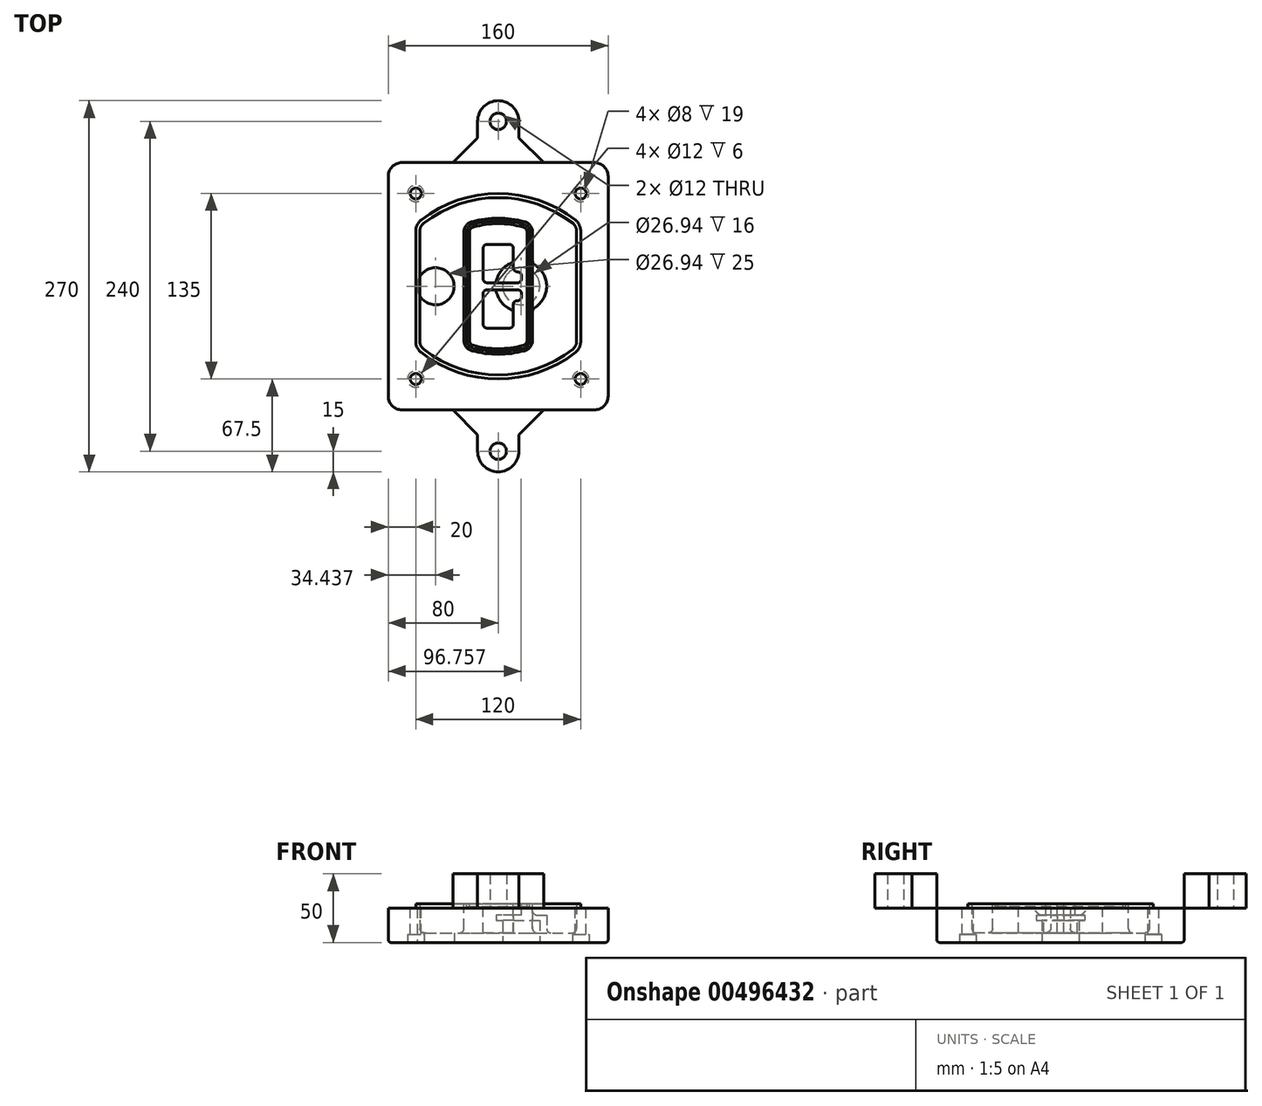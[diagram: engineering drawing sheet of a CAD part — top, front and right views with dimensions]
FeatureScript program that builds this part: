
annotation { "Feature Type Name" : "Feature", "Feature Type Description" : "" }
export const myFeature = defineFeature(function(context is Context, id is Id, definition is map)
    precondition{}
    {
        {
            var Q0;
            Q0=qCreatedBy(makeId("Top.planeOp"),FACE);
            var sketch = newSketch(context, id + "F0", { "sketchPlane" : qUnion([Q0])});
            skPoint(sketch, "E0.rect.middle", {"position": v(0, 0) * mm});
            skLineSegment(sketch, "E1.bottom", {"start": v(-70, -90) * mm, "end": v(70, -90) * mm});
            skLineSegment(sketch, "E1.top", {"start": v(-70, 90) * mm, "end": v(70, 90) * mm});
            skLineSegment(sketch, "E1.left", {"start": v(-80, -80) * mm, "end": v(-80, 80) * mm});
            skLineSegment(sketch, "E1.right", {"start": v(80, -80) * mm, "end": v(80, 80) * mm});
            skLineSegment(sketch, "E2", {"start": v(-80, 90) * mm, "end": v(80, -90) * mm, "construction": true});
            skLineSegment(sketch, "E3", {"start": v(80, 90) * mm, "end": v(-80, -90) * mm, "construction": true});
            skCircle(sketch, "E4", {"center": v(-60, 67.5) * mm, "radius": 4 * mm});
            skCircle(sketch, "E5", {"center": v(60, 67.5) * mm, "radius": 4 * mm});
            skCircle(sketch, "E6", {"center": v(60, -67.5) * mm, "radius": 4 * mm});
            skCircle(sketch, "E7", {"center": v(-60, -67.5) * mm, "radius": 4 * mm});
            skLineSegment(sketch, "E8", {"start": v(-60, 67.5) * mm, "end": v(60, 67.5) * mm, "construction": true});
            skLineSegment(sketch, "E9", {"start": v(60, 67.5) * mm, "end": v(60, -67.5) * mm, "construction": true});
            skLineSegment(sketch, "E10", {"start": v(60, -67.5) * mm, "end": v(-60, -67.5) * mm, "construction": true});
            skLineSegment(sketch, "E11", {"start": v(-60, -67.5) * mm, "end": v(-60, 67.5) * mm, "construction": true});
            skLineSegment(sketch, "E12", {"start": v(-60, 40.3) * mm, "end": v(-60, -40.3) * mm});
            skLineSegment(sketch, "E13", {"start": v(60, 40.3) * mm, "end": v(60, -40.3) * mm});
            skArc(sketch, "E14", {"start": v(56.15, 48.18) * mm, "mid": v(0, 67.5) * mm, "end": v(-56.15, 48.18) * mm});
            skArc(sketch, "E15", {"start": v(-56.15, -48.18) * mm, "mid": v(0, -67.5) * mm, "end": v(56.15, -48.18) * mm});
            skLineSegment(sketch, "E16", {"start": v(-60, 0) * mm, "end": v(60, 0) * mm, "construction": true});
            skPoint(sketch, "E17.visualSharp", {"position": v(-60, -45) * mm});
            skArc(sketch, "E17.filletArc", {"start": v(-60, -40.3) * mm, "mid": v(-58.99, -44.68) * mm, "end": v(-56.15, -48.18) * mm});
            skPoint(sketch, "E18.visualSharp", {"position": v(-60, 45) * mm});
            skArc(sketch, "E18.filletArc", {"start": v(-56.15, 48.18) * mm, "mid": v(-58.99, 44.68) * mm, "end": v(-60, 40.3) * mm});
            skPoint(sketch, "E19.visualSharp", {"position": v(60, 45) * mm});
            skArc(sketch, "E19.filletArc", {"start": v(60, 40.3) * mm, "mid": v(58.99, 44.68) * mm, "end": v(56.15, 48.18) * mm});
            skPoint(sketch, "E20.visualSharp", {"position": v(60, -45) * mm});
            skArc(sketch, "E20.filletArc", {"start": v(56.15, -48.18) * mm, "mid": v(58.99, -44.68) * mm, "end": v(60, -40.3) * mm});
            skPoint(sketch, "E21.visualSharp", {"position": v(-80, 90) * mm});
            skArc(sketch, "E21.filletArc", {"start": v(-70, 90) * mm, "mid": v(-77.07, 87.07) * mm, "end": v(-80, 80) * mm});
            skPoint(sketch, "E22.visualSharp", {"position": v(80, 90) * mm});
            skArc(sketch, "E22.filletArc", {"start": v(80, 80) * mm, "mid": v(77.07, 87.07) * mm, "end": v(70, 90) * mm});
            skPoint(sketch, "E23.visualSharp", {"position": v(80, -90) * mm});
            skArc(sketch, "E23.filletArc", {"start": v(70, -90) * mm, "mid": v(77.07, -87.07) * mm, "end": v(80, -80) * mm});
            skPoint(sketch, "E24.visualSharp", {"position": v(-80, -90) * mm});
            skArc(sketch, "E24.filletArc", {"start": v(-80, -80) * mm, "mid": v(-77.07, -87.07) * mm, "end": v(-70, -90) * mm});
            skArc(sketch, "E25.0", {"start": v(57, 40.3) * mm, "mid": v(56.3, 43.36) * mm, "end": v(54.3, 45.81) * mm});
            skLineSegment(sketch, "E25.1", {"start": v(57, 40.3) * mm, "end": v(57, -40.3) * mm});
            skArc(sketch, "E25.2", {"start": v(54.3, -45.81) * mm, "mid": v(56.3, -43.36) * mm, "end": v(57, -40.3) * mm});
            skArc(sketch, "E25.3", {"start": v(-54.3, -45.81) * mm, "mid": v(0, -64.5) * mm, "end": v(54.3, -45.81) * mm});
            skArc(sketch, "E25.4", {"start": v(-57, -40.3) * mm, "mid": v(-56.3, -43.36) * mm, "end": v(-54.3, -45.81) * mm});
            skArc(sketch, "E25.5", {"start": v(54.3, 45.81) * mm, "mid": v(0, 64.5) * mm, "end": v(-54.3, 45.81) * mm});
            skLineSegment(sketch, "E25.6", {"start": v(-57, 40.3) * mm, "end": v(-57, -40.3) * mm});
            skArc(sketch, "E25.7", {"start": v(-54.3, 45.81) * mm, "mid": v(-56.3, 43.36) * mm, "end": v(-57, 40.3) * mm});
            skArc(sketch, "E26.0", {"start": v(-58.62, 51.33) * mm, "mid": v(-62.58, 46.43) * mm, "end": v(-64, 40.3) * mm});
            skArc(sketch, "E26.1", {"start": v(58.62, 51.33) * mm, "mid": v(0, 71.5) * mm, "end": v(-58.62, 51.33) * mm});
            skArc(sketch, "E26.2", {"start": v(64, 40.3) * mm, "mid": v(62.58, 46.43) * mm, "end": v(58.62, 51.33) * mm});
            skLineSegment(sketch, "E26.3", {"start": v(64, 40.3) * mm, "end": v(64, -40.3) * mm});
            skArc(sketch, "E26.4", {"start": v(58.62, -51.33) * mm, "mid": v(62.58, -46.43) * mm, "end": v(64, -40.3) * mm});
            skLineSegment(sketch, "E26.5", {"start": v(-64, 40.3) * mm, "end": v(-64, -40.3) * mm});
            skArc(sketch, "E26.6", {"start": v(-58.62, -51.33) * mm, "mid": v(0, -71.5) * mm, "end": v(58.62, -51.33) * mm});
            skArc(sketch, "E26.7", {"start": v(-64, -40.3) * mm, "mid": v(-62.58, -46.43) * mm, "end": v(-58.62, -51.33) * mm});
            skSolve(sketch);
        }
        {
            var Q0;
            Q0=makeQuery(id+"F0.imprint","IMPRINT",FACE,{"disambiguationData":[TD([[makeQuery(id+"F0.imprint","IMPRINT",EDGE,{"derivedFrom":sQuery(id+"F0.wireOp",EDGE,"E1.bottom")}),1.0]])]});
            var Q1;
            Q1=makeQuery(id+"F0.imprint","IMPRINT",FACE,{"disambiguationData":[TD([[makeQuery(id+"F0.imprint","IMPRINT",EDGE,{"derivedFrom":sQuery(id+"F0.wireOp",EDGE,"E12")}),1.0]])]});
            var Q2;
            Q2=makeQuery(id+"F0.imprint","IMPRINT",FACE,{"disambiguationData":[TD([[makeQuery(id+"F0.imprint","IMPRINT",EDGE,{"derivedFrom":sQuery(id+"F0.wireOp",EDGE,"E25.0")}),1.0]])]});
            var Q3;
            Q3=makeQuery(id+"F0.imprint","IMPRINT",FACE,{"disambiguationData":[TD([[makeQuery(id+"F0.imprint","IMPRINT",EDGE,{"derivedFrom":sQuery(id+"F0.wireOp",EDGE,"E12")}),-1.0]])]});
            extrude(context, id + "F1", {"entities" : qUnion([Q0, Q1, Q2, Q3]), "oppositeDirection" : true, "depth" : 25 * mm});
        }
        {
            var Q0;
            Q0=makeQuery(id+"F0.imprint","IMPRINT",FACE,{"disambiguationData":[TD([[makeQuery(id+"F0.imprint","IMPRINT",EDGE,{"derivedFrom":sQuery(id+"F0.wireOp",EDGE,"E12")}),1.0]])]});
            extrude(context, id + "F2", {"entities" : qUnion([Q0]), "operationType" : NewBodyOperationType.ADD, "depth" : 3 * mm});
        }
        {
            var Q0;
            Q0=makeQuery(id+"F0.imprint","IMPRINT",FACE,{"disambiguationData":[TD([[makeQuery(id+"F0.imprint","IMPRINT",EDGE,{"derivedFrom":sQuery(id+"F0.wireOp",EDGE,"E25.0")}),1.0]])]});
            extrude(context, id + "F3", {"entities" : qUnion([Q0]), "operationType" : NewBodyOperationType.REMOVE, "oppositeDirection" : true, "depth" : 18 * mm});
        }
        {
            var Q0;
            Q0=makeQuery(id+"F2.opExtrude","CAP_FACE",FACE,{"disambiguationData":[OSD([sQuery(id+"F0.wireOp",EDGE,"E12"),sQuery(id+"F0.wireOp",EDGE,"E13"),sQuery(id+"F0.wireOp",EDGE,"E14"),sQuery(id+"F0.wireOp",EDGE,"E15"),sQuery(id+"F0.wireOp",EDGE,"E17.filletArc"),sQuery(id+"F0.wireOp",EDGE,"E18.filletArc"),sQuery(id+"F0.wireOp",EDGE,"E19.filletArc"),sQuery(id+"F0.wireOp",EDGE,"E20.filletArc"),sQuery(id+"F0.wireOp",EDGE,"E25.0"),sQuery(id+"F0.wireOp",EDGE,"E25.1"),sQuery(id+"F0.wireOp",EDGE,"E25.2"),sQuery(id+"F0.wireOp",EDGE,"E25.3"),sQuery(id+"F0.wireOp",EDGE,"E25.4"),sQuery(id+"F0.wireOp",EDGE,"E25.5"),sQuery(id+"F0.wireOp",EDGE,"E25.6"),sQuery(id+"F0.wireOp",EDGE,"E25.7")])],"isStart":false});
            var sketch = newSketch(context, id + "F4", { "sketchPlane" : qUnion([Q0])});
            skArc(sketch, "E27.0", {"start": v(-19.08, -46.97) * mm, "mid": v(0, -49.5) * mm, "end": v(19.08, -46.97) * mm});
            skArc(sketch, "E28.0", {"start": v(19.08, 46.97) * mm, "mid": v(0, 49.5) * mm, "end": v(-19.08, 46.97) * mm});
            skLineSegment(sketch, "E29", {"start": v(-25, 39.25) * mm, "end": v(-25, -39.25) * mm});
            skLineSegment(sketch, "E30", {"start": v(25, 39.25) * mm, "end": v(25, -39.25) * mm});
            skLineSegment(sketch, "E31", {"start": v(-25, 45.1) * mm, "end": v(25, 45.1) * mm, "construction": true});
            skLineSegment(sketch, "E32", {"start": v(-25, -45.1) * mm, "end": v(25, -45.1) * mm, "construction": true});
            skPoint(sketch, "E33.visualSharp", {"position": v(-25, 45.1) * mm});
            skArc(sketch, "E33.filletArc", {"start": v(-19.08, 46.97) * mm, "mid": v(-23.35, 44.11) * mm, "end": v(-25, 39.25) * mm});
            skPoint(sketch, "E34.visualSharp", {"position": v(25, 45.1) * mm});
            skArc(sketch, "E34.filletArc", {"start": v(25, 39.25) * mm, "mid": v(23.35, 44.11) * mm, "end": v(19.08, 46.97) * mm});
            skPoint(sketch, "E35.visualSharp", {"position": v(25, -45.1) * mm});
            skArc(sketch, "E35.filletArc", {"start": v(19.08, -46.97) * mm, "mid": v(23.35, -44.11) * mm, "end": v(25, -39.25) * mm});
            skPoint(sketch, "E36.visualSharp", {"position": v(-25, -45.1) * mm});
            skArc(sketch, "E36.filletArc", {"start": v(-25, -39.25) * mm, "mid": v(-23.35, -44.11) * mm, "end": v(-19.08, -46.97) * mm});
            skArc(sketch, "E37.0", {"start": v(54.3, 45.81) * mm, "mid": v(0, 64.5) * mm, "end": v(-54.3, 45.81) * mm});
            skArc(sketch, "E37.1", {"start": v(-54.3, 45.81) * mm, "mid": v(-56.3, 43.36) * mm, "end": v(-57, 40.3) * mm});
            skLineSegment(sketch, "E37.2", {"start": v(-57, 40.3) * mm, "end": v(-57, -40.3) * mm});
            skArc(sketch, "E37.3", {"start": v(-57, -40.3) * mm, "mid": v(-56.3, -43.36) * mm, "end": v(-54.3, -45.81) * mm});
            skArc(sketch, "E37.4", {"start": v(-54.3, -45.81) * mm, "mid": v(0, -64.5) * mm, "end": v(54.3, -45.81) * mm});
            skArc(sketch, "E37.5", {"start": v(54.3, -45.81) * mm, "mid": v(56.3, -43.36) * mm, "end": v(57, -40.3) * mm});
            skLineSegment(sketch, "E37.6", {"start": v(57, 40.3) * mm, "end": v(57, -40.3) * mm});
            skArc(sketch, "E37.7", {"start": v(57, 40.3) * mm, "mid": v(56.3, 43.36) * mm, "end": v(54.3, 45.81) * mm});
            skLineSegment(sketch, "E38.0", {"start": v(23, 39.25) * mm, "end": v(23, -39.25) * mm});
            skArc(sketch, "E38.1", {"start": v(18.56, -45.04) * mm, "mid": v(21.76, -42.9) * mm, "end": v(23, -39.25) * mm});
            skArc(sketch, "E38.2", {"start": v(-18.56, -45.04) * mm, "mid": v(0, -47.5) * mm, "end": v(18.56, -45.04) * mm});
            skArc(sketch, "E38.3", {"start": v(-23, -39.25) * mm, "mid": v(-21.76, -42.9) * mm, "end": v(-18.56, -45.04) * mm});
            skLineSegment(sketch, "E38.4", {"start": v(-23, 39.25) * mm, "end": v(-23, -39.25) * mm});
            skArc(sketch, "E38.5", {"start": v(23, 39.25) * mm, "mid": v(21.76, 42.9) * mm, "end": v(18.56, 45.04) * mm});
            skArc(sketch, "E38.6", {"start": v(-18.56, 45.04) * mm, "mid": v(-21.76, 42.9) * mm, "end": v(-23, 39.25) * mm});
            skArc(sketch, "E38.7", {"start": v(18.56, 45.04) * mm, "mid": v(0, 47.5) * mm, "end": v(-18.56, 45.04) * mm});
            skArc(sketch, "E39.0", {"start": v(21, 39.25) * mm, "mid": v(20.18, 41.68) * mm, "end": v(18.04, 43.1) * mm});
            skLineSegment(sketch, "E39.1", {"start": v(21, 39.25) * mm, "end": v(21, -39.25) * mm});
            skArc(sketch, "E39.2", {"start": v(18.04, -43.1) * mm, "mid": v(20.18, -41.68) * mm, "end": v(21, -39.25) * mm});
            skArc(sketch, "E39.3", {"start": v(-18.04, -43.1) * mm, "mid": v(0, -45.5) * mm, "end": v(18.04, -43.1) * mm});
            skArc(sketch, "E39.4", {"start": v(-21, -39.25) * mm, "mid": v(-20.18, -41.68) * mm, "end": v(-18.04, -43.1) * mm});
            skArc(sketch, "E39.5", {"start": v(18.04, 43.1) * mm, "mid": v(0, 45.5) * mm, "end": v(-18.04, 43.1) * mm});
            skLineSegment(sketch, "E39.6", {"start": v(-21, 39.25) * mm, "end": v(-21, -39.25) * mm});
            skArc(sketch, "E39.7", {"start": v(-18.04, 43.1) * mm, "mid": v(-20.18, 41.68) * mm, "end": v(-21, 39.25) * mm});
            skLineSegment(sketch, "E40", {"start": v(-25, 0) * mm, "end": v(25, 0) * mm, "construction": true});
            skLineSegment(sketch, "E41", {"start": v(-11, 5.5) * mm, "end": v(-11, 27.5) * mm});
            skLineSegment(sketch, "E42", {"start": v(-8, 30.5) * mm, "end": v(8, 30.5) * mm});
            skLineSegment(sketch, "E43", {"start": v(11, 27.5) * mm, "end": v(11, 13.5) * mm});
            skLineSegment(sketch, "E44", {"start": v(14, 10.5) * mm, "end": v(14, 10.5) * mm});
            skLineSegment(sketch, "E45", {"start": v(17, 7.5) * mm, "end": v(17, 5.5) * mm});
            skLineSegment(sketch, "E46", {"start": v(14, 2.5) * mm, "end": v(-8, 2.5) * mm});
            skPoint(sketch, "E47.visualSharp", {"position": v(-11, 30.5) * mm});
            skArc(sketch, "E47.filletArc", {"start": v(-8, 30.5) * mm, "mid": v(-10.12, 29.62) * mm, "end": v(-11, 27.5) * mm});
            skPoint(sketch, "E48.visualSharp", {"position": v(11, 30.5) * mm});
            skArc(sketch, "E48.filletArc", {"start": v(11, 27.5) * mm, "mid": v(10.12, 29.62) * mm, "end": v(8, 30.5) * mm});
            skPoint(sketch, "E49.visualSharp", {"position": v(11, 10.5) * mm});
            skArc(sketch, "E49.filletArc", {"start": v(11, 13.5) * mm, "mid": v(11.88, 11.38) * mm, "end": v(14, 10.5) * mm});
            skPoint(sketch, "E50.visualSharp", {"position": v(17, 10.5) * mm});
            skArc(sketch, "E50.filletArc", {"start": v(17, 7.5) * mm, "mid": v(16.12, 9.62) * mm, "end": v(14, 10.5) * mm});
            skPoint(sketch, "E51.visualSharp", {"position": v(17, 2.5) * mm});
            skArc(sketch, "E51.filletArc", {"start": v(14, 2.5) * mm, "mid": v(16.12, 3.38) * mm, "end": v(17, 5.5) * mm});
            skPoint(sketch, "E52.visualSharp", {"position": v(-11, 2.5) * mm});
            skArc(sketch, "E52.filletArc", {"start": v(-11, 5.5) * mm, "mid": v(-10.12, 3.38) * mm, "end": v(-8, 2.5) * mm});
            skLineSegment(sketch, "E53.0.MirrorCS", {"start": v(14, -2.5) * mm, "end": v(-8, -2.5) * mm});
            skArc(sketch, "E54.0.MirrorCS", {"start": v(-11, -5.5) * mm, "mid": v(-10.12, -3.38) * mm, "end": v(-8, -2.5) * mm});
            skLineSegment(sketch, "E55.0.MirrorCS", {"start": v(-11, -5.5) * mm, "end": v(-11, -27.5) * mm});
            skArc(sketch, "E56.0.MirrorCS", {"start": v(-8, -30.5) * mm, "mid": v(-10.12, -29.62) * mm, "end": v(-11, -27.5) * mm});
            skLineSegment(sketch, "E57.0.MirrorCS", {"start": v(-8, -30.5) * mm, "end": v(8, -30.5) * mm});
            skArc(sketch, "E58.0.MirrorCS", {"start": v(11, -27.5) * mm, "mid": v(10.12, -29.62) * mm, "end": v(8, -30.5) * mm});
            skLineSegment(sketch, "E59.0.MirrorCS", {"start": v(11, -27.5) * mm, "end": v(11, -13.5) * mm});
            skArc(sketch, "E60.0.MirrorCS", {"start": v(11, -13.5) * mm, "mid": v(11.88, -11.38) * mm, "end": v(14, -10.5) * mm});
            skArc(sketch, "E61.0.MirrorCS", {"start": v(17, -7.5) * mm, "mid": v(16.12, -9.62) * mm, "end": v(14, -10.5) * mm});
            skLineSegment(sketch, "E62.0.MirrorCS", {"start": v(17, -7.5) * mm, "end": v(17, -5.5) * mm});
            skArc(sketch, "E63.0.MirrorCS", {"start": v(14, -2.5) * mm, "mid": v(16.12, -3.38) * mm, "end": v(17, -5.5) * mm});
            skSolve(sketch);
        }
        {
            var Q0;
            Q0=makeQuery(id+"F4.imprint","IMPRINT",FACE,{"disambiguationData":[TD([[makeQuery(id+"F4.imprint","IMPRINT",EDGE,{"derivedFrom":sQuery(id+"F4.wireOp",EDGE,"E27.0")}),1.0]])]});
            var Q1;
            Q1=makeQuery(id+"F4.imprint","IMPRINT",FACE,{"disambiguationData":[TD([[makeQuery(id+"F4.imprint","IMPRINT",EDGE,{"derivedFrom":sQuery(id+"F4.wireOp",EDGE,"E38.0")}),-1.0]])]});
            var Q2;
            Q2=makeQuery(id+"F4.imprint","IMPRINT",FACE,{"disambiguationData":[TD([[makeQuery(id+"F4.imprint","IMPRINT",EDGE,{"derivedFrom":sQuery(id+"F4.wireOp",EDGE,"E39.0")}),1.0]])]});
            extrude(context, id + "F5", {"entities" : qUnion([Q0, Q1, Q2]), "operationType" : NewBodyOperationType.ADD, "endBound" : BoundingType.UP_TO_NEXT, "oppositeDirection" : true, "depth" : 25 * mm});
        }
        {
            var Q0;
            Q0=makeQuery(id+"F4.imprint","IMPRINT",FACE,{"disambiguationData":[TD([[makeQuery(id+"F4.imprint","IMPRINT",EDGE,{"derivedFrom":sQuery(id+"F4.wireOp",EDGE,"E38.0")}),-1.0]])]});
            extrude(context, id + "F6", {"entities" : qUnion([Q0]), "operationType" : NewBodyOperationType.REMOVE, "oppositeDirection" : true, "depth" : 2 * mm});
        }
        {
            var Q0;
            Q0=makeQuery(id+"F1.opExtrude","CAP_FACE",FACE,{"disambiguationData":[OSD([sQuery(id+"F0.wireOp",EDGE,"E1.bottom"),sQuery(id+"F0.wireOp",EDGE,"E1.top"),sQuery(id+"F0.wireOp",EDGE,"E1.left"),sQuery(id+"F0.wireOp",EDGE,"E1.right"),sQuery(id+"F0.wireOp",EDGE,"E4"),sQuery(id+"F0.wireOp",EDGE,"E5"),sQuery(id+"F0.wireOp",EDGE,"E6"),sQuery(id+"F0.wireOp",EDGE,"E7"),sQuery(id+"F0.wireOp",EDGE,"E21.filletArc"),sQuery(id+"F0.wireOp",EDGE,"E22.filletArc"),sQuery(id+"F0.wireOp",EDGE,"E23.filletArc"),sQuery(id+"F0.wireOp",EDGE,"E24.filletArc")])],"isStart":false});
            var sketch = newSketch(context, id + "F7", { "sketchPlane" : qUnion([Q0])});
            skCircle(sketch, "E64", {"center": v(16.76, 0) * mm, "radius": 13.47 * mm});
            skCircle(sketch, "E65", {"center": v(-45.56, 0) * mm, "radius": 13.47 * mm});
            skLineSegment(sketch, "E66", {"start": v(80, 0) * mm, "end": v(-80, 0) * mm});
            skCircle(sketch, "E67", {"center": v(16.76, 0) * mm, "radius": 18.47 * mm});
            skCircle(sketch, "E68", {"center": v(60, -67.5) * mm, "radius": 6 * mm});
            skCircle(sketch, "E69", {"center": v(-60, -67.5) * mm, "radius": 6 * mm});
            skCircle(sketch, "E70", {"center": v(-60, 67.5) * mm, "radius": 6 * mm});
            skCircle(sketch, "E71", {"center": v(60, 67.5) * mm, "radius": 6 * mm});
            skSolve(sketch);
        }
        {
            var Q0;
            {var subQ1=sQuery(id+"F7.wireOp",EDGE,"E66");var subQ4=sQuery(id+"F7.wireOp",EDGE,"E64");var subQ6=makeQuery(id+"F7.imprint","INTERSECT",VERTEX,{"disambiguationData":[OD(0.0)],"derivedFrom":[subQ4,subQ1]});Q0=makeQuery(id+"F7.imprint","IMPRINT",FACE,{"disambiguationData":[TD([[makeQuery(id+"F7.imprint","IMPRINT",EDGE,{"disambiguationData":[TD([[subQ6,-1.0]])],"derivedFrom":subQ4}),-1.0]])]});}
            var Q1;
            {var subQ0=sQuery(id+"F7.wireOp",EDGE,"E66");var subQ1=sQuery(id+"F7.wireOp",EDGE,"E64");var subQ3=makeQuery(id+"F7.imprint","INTERSECT",VERTEX,{"disambiguationData":[OD(0.0)],"derivedFrom":[subQ1,subQ0]});Q1=makeQuery(id+"F7.imprint","IMPRINT",FACE,{"disambiguationData":[TD([[makeQuery(id+"F7.imprint","IMPRINT",EDGE,{"disambiguationData":[TD([[subQ3,-1.0]])],"derivedFrom":subQ1}),1.0]])]});}
            var Q2;
            {var subQ0=sQuery(id+"F7.wireOp",EDGE,"E66");var subQ1=sQuery(id+"F7.wireOp",EDGE,"E64");var subQ3=makeQuery(id+"F7.imprint","INTERSECT",VERTEX,{"disambiguationData":[OD(0.0)],"derivedFrom":[subQ1,subQ0]});Q2=makeQuery(id+"F7.imprint","IMPRINT",FACE,{"disambiguationData":[TD([[makeQuery(id+"F7.imprint","IMPRINT",EDGE,{"disambiguationData":[TD([[subQ3,1.0]])],"derivedFrom":subQ1}),1.0]])]});}
            var Q3;
            {var subQ1=sQuery(id+"F7.wireOp",EDGE,"E66");var subQ4=sQuery(id+"F7.wireOp",EDGE,"E64");var subQ6=makeQuery(id+"F7.imprint","INTERSECT",VERTEX,{"disambiguationData":[OD(0.0)],"derivedFrom":[subQ4,subQ1]});Q3=makeQuery(id+"F7.imprint","IMPRINT",FACE,{"disambiguationData":[TD([[makeQuery(id+"F7.imprint","IMPRINT",EDGE,{"disambiguationData":[TD([[subQ6,1.0]])],"derivedFrom":subQ4}),-1.0]])]});}
            extrude(context, id + "F8", {"entities" : qUnion([Q0, Q1, Q2, Q3]), "operationType" : NewBodyOperationType.ADD, "oppositeDirection" : true, "depth" : 20 * mm});
        }
        {
            var Q0;
            {var subQ0=sQuery(id+"F7.wireOp",EDGE,"E66");var subQ1=sQuery(id+"F7.wireOp",EDGE,"E64");var subQ3=makeQuery(id+"F7.imprint","INTERSECT",VERTEX,{"disambiguationData":[OD(0.0)],"derivedFrom":[subQ1,subQ0]});Q0=makeQuery(id+"F7.imprint","IMPRINT",FACE,{"disambiguationData":[TD([[makeQuery(id+"F7.imprint","IMPRINT",EDGE,{"disambiguationData":[TD([[subQ3,-1.0]])],"derivedFrom":subQ1}),1.0]])]});}
            var Q1;
            {var subQ0=sQuery(id+"F7.wireOp",EDGE,"E66");var subQ1=sQuery(id+"F7.wireOp",EDGE,"E64");var subQ3=makeQuery(id+"F7.imprint","INTERSECT",VERTEX,{"disambiguationData":[OD(0.0)],"derivedFrom":[subQ1,subQ0]});Q1=makeQuery(id+"F7.imprint","IMPRINT",FACE,{"disambiguationData":[TD([[makeQuery(id+"F7.imprint","IMPRINT",EDGE,{"disambiguationData":[TD([[subQ3,1.0]])],"derivedFrom":subQ1}),1.0]])]});}
            extrude(context, id + "F9", {"entities" : qUnion([Q0, Q1]), "operationType" : NewBodyOperationType.REMOVE, "oppositeDirection" : true, "depth" : 16 * mm});
        }
        {
            var Q0;
            {var subQ0=sQuery(id+"F7.wireOp",EDGE,"E66");var subQ1=sQuery(id+"F7.wireOp",EDGE,"E65");var subQ3=makeQuery(id+"F7.imprint","INTERSECT",VERTEX,{"disambiguationData":[OD(0.0)],"derivedFrom":[subQ1,subQ0]});Q0=makeQuery(id+"F7.imprint","IMPRINT",FACE,{"disambiguationData":[TD([[makeQuery(id+"F7.imprint","IMPRINT",EDGE,{"disambiguationData":[TD([[subQ3,-1.0]])],"derivedFrom":subQ1}),1.0]])]});}
            var Q1;
            {var subQ0=sQuery(id+"F7.wireOp",EDGE,"E66");var subQ1=sQuery(id+"F7.wireOp",EDGE,"E65");var subQ3=makeQuery(id+"F7.imprint","INTERSECT",VERTEX,{"disambiguationData":[OD(0.0)],"derivedFrom":[subQ1,subQ0]});Q1=makeQuery(id+"F7.imprint","IMPRINT",FACE,{"disambiguationData":[TD([[makeQuery(id+"F7.imprint","IMPRINT",EDGE,{"disambiguationData":[TD([[subQ3,1.0]])],"derivedFrom":subQ1}),1.0]])]});}
            var Q2;
            Q2 = qSketchRegion(id + "F16", true);
            extrude(context, id + "F10", {"entities" : qUnion([Q0, Q1, Q2]), "operationType" : NewBodyOperationType.REMOVE, "oppositeDirection" : true, "depth" : 25 * mm});
        }
        {
            var Q0;
            Q0=makeQuery(id+"F7.imprint","IMPRINT",FACE,{"disambiguationData":[TD([[makeQuery(id+"F7.imprint","IMPRINT",EDGE,{"derivedFrom":sQuery(id+"F7.wireOp",EDGE,"E68")}),1.0]])]});
            var Q1;
            Q1=makeQuery(id+"F7.imprint","IMPRINT",FACE,{"disambiguationData":[TD([[makeQuery(id+"F7.imprint","IMPRINT",EDGE,{"derivedFrom":makeQuery(id+"F1.opExtrude","CAP_EDGE",EDGE,{"disambiguationData":[OSD([sQuery(id+"F0.wireOp",EDGE,"E5")])],"isStart":false})}),-1.0]])]});
            var Q2;
            Q2=makeQuery(id+"F7.imprint","IMPRINT",FACE,{"disambiguationData":[TD([[makeQuery(id+"F7.imprint","IMPRINT",EDGE,{"derivedFrom":sQuery(id+"F7.wireOp",EDGE,"E69")}),1.0]])]});
            var Q3;
            Q3=makeQuery(id+"F7.imprint","IMPRINT",FACE,{"disambiguationData":[TD([[makeQuery(id+"F7.imprint","IMPRINT",EDGE,{"derivedFrom":makeQuery(id+"F1.opExtrude","CAP_EDGE",EDGE,{"disambiguationData":[OSD([sQuery(id+"F0.wireOp",EDGE,"E4")])],"isStart":false})}),-1.0]])]});
            var Q4;
            Q4=makeQuery(id+"F7.imprint","IMPRINT",FACE,{"disambiguationData":[TD([[makeQuery(id+"F7.imprint","IMPRINT",EDGE,{"derivedFrom":sQuery(id+"F7.wireOp",EDGE,"E70")}),1.0]])]});
            var Q5;
            Q5=makeQuery(id+"F7.imprint","IMPRINT",FACE,{"disambiguationData":[TD([[makeQuery(id+"F7.imprint","IMPRINT",EDGE,{"derivedFrom":makeQuery(id+"F1.opExtrude","CAP_EDGE",EDGE,{"disambiguationData":[OSD([sQuery(id+"F0.wireOp",EDGE,"E7")])],"isStart":false})}),-1.0]])]});
            var Q6;
            Q6=makeQuery(id+"F7.imprint","IMPRINT",FACE,{"disambiguationData":[TD([[makeQuery(id+"F7.imprint","IMPRINT",EDGE,{"derivedFrom":sQuery(id+"F7.wireOp",EDGE,"E71")}),1.0]])]});
            var Q7;
            Q7=makeQuery(id+"F7.imprint","IMPRINT",FACE,{"disambiguationData":[TD([[makeQuery(id+"F7.imprint","IMPRINT",EDGE,{"derivedFrom":makeQuery(id+"F1.opExtrude","CAP_EDGE",EDGE,{"disambiguationData":[OSD([sQuery(id+"F0.wireOp",EDGE,"E6")])],"isStart":false})}),-1.0]])]});
            extrude(context, id + "F11", {"entities" : qUnion([Q0, Q1, Q2, Q3, Q4, Q5, Q6, Q7]), "operationType" : NewBodyOperationType.REMOVE, "oppositeDirection" : true, "depth" : 6 * mm});
        }
        {
            var Q0;
            Q0=makeQuery(id+"F9.boolean.opBoolean","COPY",FACE,{"derivedFrom":makeQuery(id+"F9.opExtrude","CAP_FACE",FACE,{"disambiguationData":[OSD([sQuery(id+"F7.wireOp",EDGE,"E64")])],"isStart":false})});
            var sketch = newSketch(context, id + "F12", { "sketchPlane" : qUnion([Q0])});
            skArc(sketch, "E72.0", {"start": v(11, 17.55) * mm, "mid": v(2.57, 11.82) * mm, "end": v(-1.54, 2.5) * mm});
            skArc(sketch, "E72.1", {"start": v(-1.54, -2.5) * mm, "mid": v(2.57, -11.82) * mm, "end": v(11, -17.55) * mm});
            skLineSegment(sketch, "E73", {"start": v(-1.54, -2.5) * mm, "end": v(14, -2.5) * mm});
            skLineSegment(sketch, "E74.0", {"start": v(14, 2.5) * mm, "end": v(-1.54, 2.5) * mm});
            skArc(sketch, "E74.1", {"start": v(14, 2.5) * mm, "mid": v(16.12, 3.38) * mm, "end": v(17, 5.5) * mm});
            skLineSegment(sketch, "E74.2", {"start": v(17, 7.5) * mm, "end": v(17, 5.5) * mm});
            skArc(sketch, "E74.3", {"start": v(17, 7.5) * mm, "mid": v(16.12, 9.62) * mm, "end": v(14, 10.5) * mm});
            skArc(sketch, "E74.4", {"start": v(11, 13.5) * mm, "mid": v(11.88, 11.38) * mm, "end": v(14, 10.5) * mm});
            skLineSegment(sketch, "E74.5", {"start": v(11, 17.55) * mm, "end": v(11, 13.5) * mm});
            skLineSegment(sketch, "E74.7", {"start": v(14, -2.5) * mm, "end": v(-1.54, -2.5) * mm});
            skArc(sketch, "E74.8", {"start": v(14, -2.5) * mm, "mid": v(16.12, -3.38) * mm, "end": v(17, -5.5) * mm});
            skLineSegment(sketch, "E74.9", {"start": v(17, -7.5) * mm, "end": v(17, -5.5) * mm});
            skArc(sketch, "E74.10", {"start": v(17, -7.5) * mm, "mid": v(16.12, -9.62) * mm, "end": v(14, -10.5) * mm});
            skArc(sketch, "E74.11", {"start": v(11, -13.5) * mm, "mid": v(11.88, -11.38) * mm, "end": v(14, -10.5) * mm});
            skLineSegment(sketch, "E74.12", {"start": v(11, -17.55) * mm, "end": v(11, -13.5) * mm});
            skPoint(sketch, "E75.orphan", {"position": v(11, -27.5) * mm});
            skPoint(sketch, "E76.orphan", {"position": v(-8, -2.5) * mm});
            skPoint(sketch, "E77.orphan", {"position": v(-8, 2.5) * mm});
            skPoint(sketch, "E78.orphan", {"position": v(11, 27.5) * mm});
            skSolve(sketch);
        }
        {
            var Q0;
            {var subQ7=sQuery(id+"F12.wireOp",EDGE,"E72.0");var subQ14=sQuery(id+"F12.wireOp",EDGE,"E72.1");var subQ16=sQuery(id+"F12.wireOp",EDGE,"E74.1");var subQ18=sQuery(id+"F12.wireOp",EDGE,"E74.8");Q0=qUnion([makeQuery(id+"F12.imprint","IMPRINT",FACE,{"disambiguationData":[TD([[makeQuery(id+"F12.imprint","IMPRINT",EDGE,{"derivedFrom":subQ7}),1.0]])]}),makeQuery(id+"F12.imprint","IMPRINT",FACE,{"disambiguationData":[TD([[makeQuery(id+"F12.imprint","IMPRINT",EDGE,{"derivedFrom":subQ14}),1.0]])]}),makeQuery(id+"F12.imprint","IMPRINT",FACE,{"disambiguationData":[TD([[makeQuery(id+"F12.imprint","IMPRINT",EDGE,{"derivedFrom":subQ16}),1.0]])]}),makeQuery(id+"F12.imprint","IMPRINT",FACE,{"disambiguationData":[TD([[makeQuery(id+"F12.imprint","IMPRINT",EDGE,{"derivedFrom":subQ18}),-1.0]])]})]);}
            var Q1;
            Q1=makeQuery(id+"F5.boolean.opBoolean","SPLIT",FACE,{"disambiguationData":[TD([makeQuery(id+"F5.opExtrude","SWEPT_FACE",FACE,{"disambiguationData":[OSD([sQuery(id+"F4.wireOp",EDGE,"E41")])]})])],"derivedFrom":makeQuery(id+"F3.boolean.opBoolean","COPY",FACE,{"derivedFrom":makeQuery(id+"F3.opExtrude","CAP_FACE",FACE,{"disambiguationData":[OSD([sQuery(id+"F0.wireOp",EDGE,"E25.0"),sQuery(id+"F0.wireOp",EDGE,"E25.1"),sQuery(id+"F0.wireOp",EDGE,"E25.2"),sQuery(id+"F0.wireOp",EDGE,"E25.3"),sQuery(id+"F0.wireOp",EDGE,"E25.4"),sQuery(id+"F0.wireOp",EDGE,"E25.5"),sQuery(id+"F0.wireOp",EDGE,"E25.6"),sQuery(id+"F0.wireOp",EDGE,"E25.7")])],"isStart":false})})});
            extrude(context, id + "F13", {"entities" : qUnion([Q0]), "operationType" : NewBodyOperationType.REMOVE, "endBound" : BoundingType.UP_TO_SURFACE, "endBoundEntityFace" : qUnion([Q1]), "depth" : 25 * mm});
        }
        {
            var Q0;
            Q0=makeQuery(id+"F3.boolean.opBoolean","COPY",EDGE,{"derivedFrom":makeQuery(id+"F3.opExtrude","CAP_EDGE",EDGE,{"disambiguationData":[OSD([sQuery(id+"F0.wireOp",EDGE,"E25.6")])],"isStart":false})});
            var Q1;
            Q1=makeQuery(id+"F8.boolean.opBoolean","INTERSECT",EDGE,{"derivedFrom":[makeQuery(id+"F5.opExtrude","SWEPT_FACE",FACE,{"disambiguationData":[OSD([sQuery(id+"F4.wireOp",EDGE,"E30")])]}),makeQuery(id+"F8.opExtrude","CAP_FACE",FACE,{"disambiguationData":[OSD([sQuery(id+"F7.wireOp",EDGE,"E67")])],"isStart":false})]});
            var Q2;
            Q2=makeQuery(id+"F8.boolean.opBoolean","INTERSECT",EDGE,{"disambiguationData":[OD(1.0)],"derivedFrom":[makeQuery(id+"F5.opExtrude","SWEPT_FACE",FACE,{"disambiguationData":[OSD([sQuery(id+"F4.wireOp",EDGE,"E30")])]}),makeQuery(id+"F8.opExtrude","SWEPT_FACE",FACE,{"disambiguationData":[OSD([sQuery(id+"F7.wireOp",EDGE,"E67")])]})]});
            var Q3;
            {var subQ0=sQuery(id+"F4.wireOp",EDGE,"E30");Q3=makeQuery(id+"F8.boolean.opBoolean","SPLIT",EDGE,{"disambiguationData":[TD([makeQuery(id+"F5.opExtrude","SWEPT_FACE",FACE,{"disambiguationData":[OSD([sQuery(id+"F4.wireOp",EDGE,"E35.filletArc")])]})])],"derivedFrom":makeQuery(id+"F5.opExtrude","CAP_EDGE",EDGE,{"disambiguationData":[OSD([subQ0])],"isStart":false})});}
            var Q4;
            {var subQ0=sQuery(id+"F0.wireOp",EDGE,"E25.7");var subQ1=sQuery(id+"F0.wireOp",EDGE,"E25.1");var subQ2=sQuery(id+"F0.wireOp",EDGE,"E25.6");var subQ3=sQuery(id+"F0.wireOp",EDGE,"E25.5");var subQ4=sQuery(id+"F0.wireOp",EDGE,"E25.4");var subQ5=sQuery(id+"F0.wireOp",EDGE,"E25.0");var subQ6=sQuery(id+"F0.wireOp",EDGE,"E25.2");var subQ7=sQuery(id+"F0.wireOp",EDGE,"E25.3");Q4=makeQuery(id+"F8.boolean.opBoolean","INTERSECT",EDGE,{"derivedFrom":[makeQuery(id+"F5.boolean.opBoolean","SPLIT",FACE,{"disambiguationData":[TD([makeQuery(id+"F2.opExtrude","SWEPT_FACE",FACE,{"disambiguationData":[OSD([subQ5])]})])],"derivedFrom":makeQuery(id+"F3.boolean.opBoolean","COPY",FACE,{"derivedFrom":makeQuery(id+"F3.opExtrude","CAP_FACE",FACE,{"disambiguationData":[OSD([subQ5,subQ1,subQ6,subQ7,subQ4,subQ3,subQ2,subQ0])],"isStart":false})})}),makeQuery(id+"F8.opExtrude","SWEPT_FACE",FACE,{"disambiguationData":[OSD([sQuery(id+"F7.wireOp",EDGE,"E67")])]})]});}
            var Q5;
            Q5=makeQuery(id+"F8.boolean.opBoolean","INTERSECT",EDGE,{"disambiguationData":[OD(0.0)],"derivedFrom":[makeQuery(id+"F5.opExtrude","SWEPT_FACE",FACE,{"disambiguationData":[OSD([sQuery(id+"F4.wireOp",EDGE,"E30")])]}),makeQuery(id+"F8.opExtrude","SWEPT_FACE",FACE,{"disambiguationData":[OSD([sQuery(id+"F7.wireOp",EDGE,"E67")])]})]});
            fillet(context, id + "F14", {"entities" : qUnion([Q0, Q1, Q2, Q3, Q4, Q5]), "radius" : 3 * mm, "tangentPropagation" : true, "allowEdgeOverflow" : false});
        }
        {
            var Q0;
            Q0=makeQuery(id+"F1.opExtrude","CAP_EDGE",EDGE,{"disambiguationData":[OSD([sQuery(id+"F0.wireOp",EDGE,"E1.bottom")])],"isStart":false});
            fillet(context, id + "F15", {"entities" : qUnion([Q0]), "radius" : 2 * mm, "tangentPropagation" : true, "allowEdgeOverflow" : false});
        }
        {
            var Q0;
            {var subQ0=sQuery(id+"F0.wireOp",EDGE,"E21.filletArc");var subQ1=sQuery(id+"F0.wireOp",EDGE,"E7");var subQ2=sQuery(id+"F0.wireOp",EDGE,"E6");var subQ3=sQuery(id+"F0.wireOp",EDGE,"E5");var subQ4=sQuery(id+"F0.wireOp",EDGE,"E4");var subQ5=sQuery(id+"F0.wireOp",EDGE,"E22.filletArc");var subQ6=sQuery(id+"F0.wireOp",EDGE,"E1.bottom");var subQ7=sQuery(id+"F0.wireOp",EDGE,"E1.right");var subQ8=sQuery(id+"F0.wireOp",EDGE,"E1.top");var subQ9=sQuery(id+"F0.wireOp",EDGE,"E1.left");var subQ10=sQuery(id+"F0.wireOp",EDGE,"E23.filletArc");var subQ11=sQuery(id+"F0.wireOp",EDGE,"E24.filletArc");Q0=makeQuery(id+"F2.boolean.opBoolean","SPLIT",FACE,{"disambiguationData":[TD([makeQuery(id+"F1.opExtrude","SWEPT_FACE",FACE,{"disambiguationData":[OSD([subQ6])]})])],"derivedFrom":makeQuery(id+"F1.opExtrude","CAP_FACE",FACE,{"disambiguationData":[OSD([subQ6,subQ8,subQ9,subQ7,subQ4,subQ3,subQ2,subQ1,subQ0,subQ5,subQ10,subQ11])],"isStart":true})});}
            var sketch = newSketch(context, id + "F16", { "sketchPlane" : qUnion([Q0])});
            skLineSegment(sketch, "E79.0", {"start": v(-70, 90) * mm, "end": v(70, 90) * mm});
            skArc(sketch, "E79.1", {"start": v(80, 80) * mm, "mid": v(77.07, 87.07) * mm, "end": v(70, 90) * mm});
            skLineSegment(sketch, "E79.2", {"start": v(80, -80) * mm, "end": v(80, 80) * mm});
            skCircle(sketch, "E79.3", {"center": v(60, 67.5) * mm, "radius": 4 * mm});
            skArc(sketch, "E79.4", {"start": v(56.15, 48.18) * mm, "mid": v(0, 67.5) * mm, "end": v(-56.15, 48.18) * mm});
            skArc(sketch, "E79.5", {"start": v(60, 40.3) * mm, "mid": v(58.99, 44.68) * mm, "end": v(56.15, 48.18) * mm});
            skLineSegment(sketch, "E79.6", {"start": v(60, 40.3) * mm, "end": v(60, -40.3) * mm});
            skCircle(sketch, "E79.7", {"center": v(-60, 67.5) * mm, "radius": 4 * mm});
            skArc(sketch, "E79.8", {"start": v(-70, 90) * mm, "mid": v(-77.07, 87.07) * mm, "end": v(-80, 80) * mm});
            skLineSegment(sketch, "E79.9", {"start": v(-80, -80) * mm, "end": v(-80, 80) * mm});
            skArc(sketch, "E79.10", {"start": v(-56.15, 48.18) * mm, "mid": v(-58.99, 44.68) * mm, "end": v(-60, 40.3) * mm});
            skLineSegment(sketch, "E79.11", {"start": v(-60, 40.3) * mm, "end": v(-60, -40.3) * mm});
            skArc(sketch, "E79.12", {"start": v(-56.15, -48.18) * mm, "mid": v(0, -67.5) * mm, "end": v(56.15, -48.18) * mm});
            skArc(sketch, "E79.13", {"start": v(56.15, -48.18) * mm, "mid": v(58.99, -44.68) * mm, "end": v(60, -40.3) * mm});
            skArc(sketch, "E79.14", {"start": v(-60, -40.3) * mm, "mid": v(-58.99, -44.68) * mm, "end": v(-56.15, -48.18) * mm});
            skCircle(sketch, "E79.15", {"center": v(-60, -67.5) * mm, "radius": 4 * mm});
            skArc(sketch, "E79.16", {"start": v(-80, -80) * mm, "mid": v(-77.07, -87.07) * mm, "end": v(-70, -90) * mm});
            skLineSegment(sketch, "E79.17", {"start": v(-70, -90) * mm, "end": v(70, -90) * mm});
            skArc(sketch, "E79.18", {"start": v(70, -90) * mm, "mid": v(77.07, -87.07) * mm, "end": v(80, -80) * mm});
            skCircle(sketch, "E79.19", {"center": v(60, -67.5) * mm, "radius": 4 * mm});
            skLineSegment(sketch, "E80", {"start": v(0, 90) * mm, "end": v(0, 120) * mm, "construction": true});
            skLineSegment(sketch, "E81", {"start": v(-33, 90) * mm, "end": v(-15, 108) * mm});
            skLineSegment(sketch, "E82", {"start": v(-15, 108) * mm, "end": v(-15, 120) * mm});
            skLineSegment(sketch, "E83", {"start": v(33, 90) * mm, "end": v(15, 108) * mm});
            skLineSegment(sketch, "E84", {"start": v(15, 108) * mm, "end": v(15, 120) * mm});
            skArc(sketch, "E85", {"start": v(15, 120) * mm, "mid": v(0, 135) * mm, "end": v(-15, 120) * mm});
            skCircle(sketch, "E86", {"center": v(0, 120) * mm, "radius": 6 * mm});
            skLineSegment(sketch, "E87", {"start": v(0, 0) * mm, "end": v(-146.2, 0) * mm, "construction": true});
            skPoint(sketch, "E87.endSnap0", {"position": v(-80, 0) * mm});
            skLineSegment(sketch, "E88", {"start": v(-146.2, 0) * mm, "end": v(0, 0) * mm, "construction": true});
            skLineSegment(sketch, "E89", {"start": v(0, 0) * mm, "end": v(142.06, 0) * mm, "construction": true});
            skLineSegment(sketch, "E90.MirrorCS", {"start": v(33, -90) * mm, "end": v(15, -108) * mm});
            skLineSegment(sketch, "E91.MirrorCS", {"start": v(15, -108) * mm, "end": v(15, -120) * mm});
            skArc(sketch, "E92.MirrorCS", {"start": v(15, -120) * mm, "mid": v(0, -135) * mm, "end": v(-15, -120) * mm});
            skCircle(sketch, "E93.MirrorC", {"center": v(0, -120) * mm, "radius": 6 * mm});
            skLineSegment(sketch, "E94.MirrorCS", {"start": v(-33, -90) * mm, "end": v(-15, -108) * mm});
            skLineSegment(sketch, "E95.MirrorCS", {"start": v(-15, -108) * mm, "end": v(-15, -120) * mm});
            skLineSegment(sketch, "E96.MirrorCS", {"start": v(0, -90) * mm, "end": v(0, -120) * mm, "construction": true});
            skSolve(sketch);
        }
        {
            var Q0;
            {var subQ0=sQuery(id+"F16.wireOp",EDGE,"E81");Q0=makeQuery(id+"F16.imprint","IMPRINT",FACE,{"disambiguationData":[TD([[makeQuery(id+"F16.imprint","IMPRINT",EDGE,{"derivedFrom":subQ0}),-1.0]])]});}
            var Q1;
            {var subQ0=sQuery(id+"F16.wireOp",EDGE,"E90.MirrorCS");Q1=makeQuery(id+"F16.imprint","IMPRINT",FACE,{"disambiguationData":[TD([[makeQuery(id+"F16.imprint","IMPRINT",EDGE,{"derivedFrom":subQ0}),-1.0]])]});}
            extrude(context, id + "F17", {"entities" : qUnion([Q0, Q1]), "depth" : 25 * mm});
        }
    });
